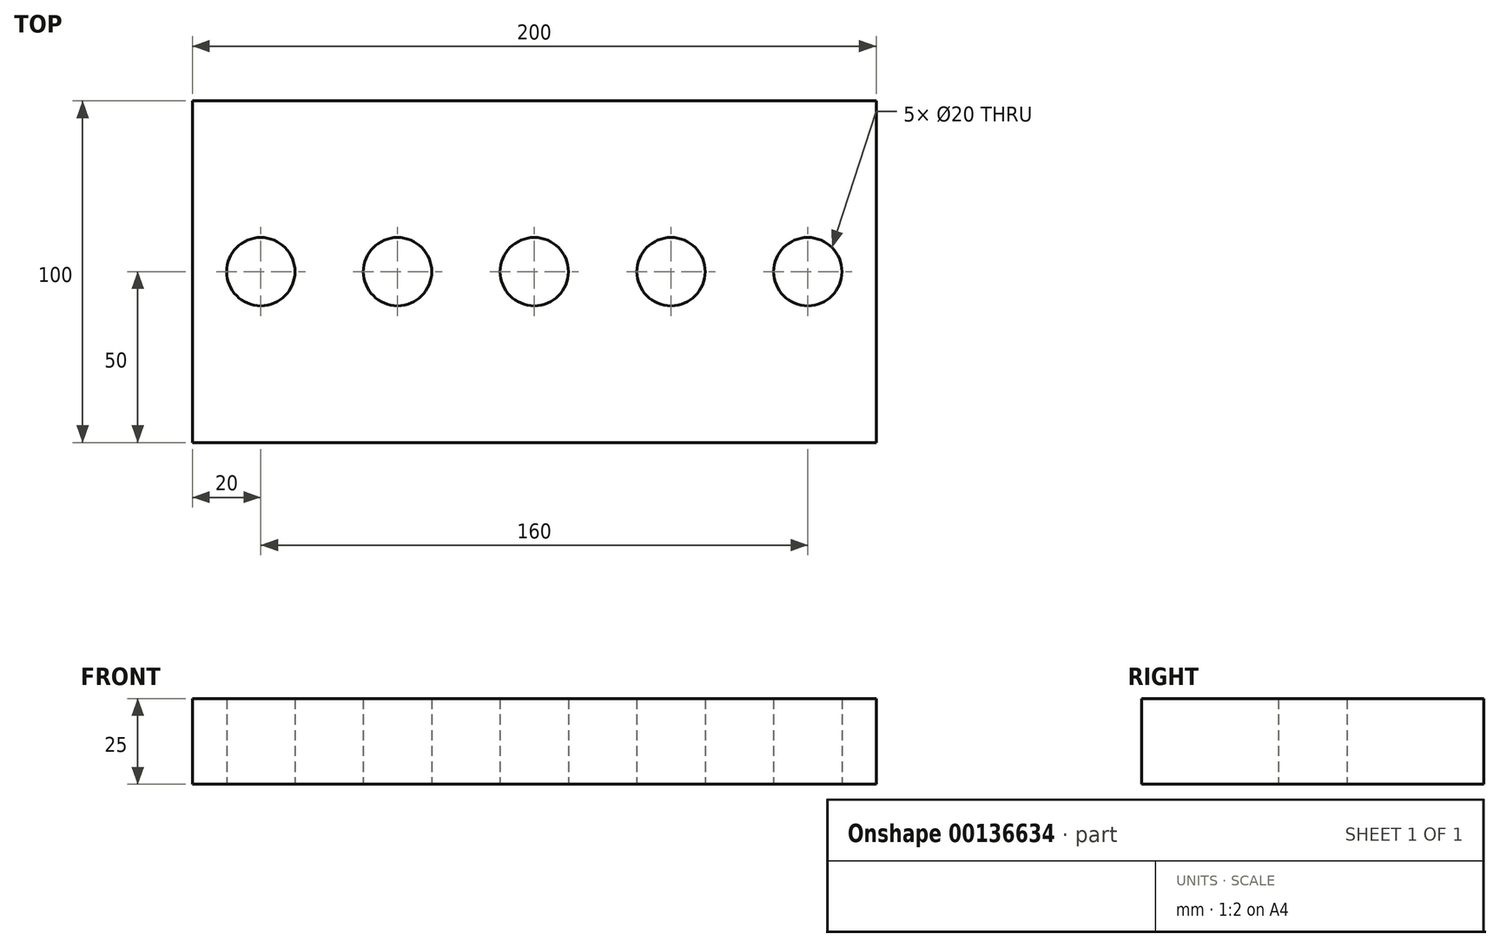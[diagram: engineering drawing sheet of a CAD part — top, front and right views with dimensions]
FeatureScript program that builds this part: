
annotation { "Feature Type Name" : "Feature", "Feature Type Description" : "" }
export const myFeature = defineFeature(function(context is Context, id is Id, definition is map)
    precondition{}
    {
        {
            var Q0;
            Q0=qCreatedBy(makeId("Top.planeOp"),FACE);
            var sketch = newSketch(context, id + "F0", { "sketchPlane" : qUnion([Q0])});
            skLineSegment(sketch, "E0.bottom", {"start": v(-100, 50) * mm, "end": v(100, 50) * mm});
            skLineSegment(sketch, "E0.top", {"start": v(-100, -50) * mm, "end": v(100, -50) * mm});
            skLineSegment(sketch, "E0.left", {"start": v(-100, 50) * mm, "end": v(-100, -50) * mm});
            skLineSegment(sketch, "E0.right", {"start": v(100, 50) * mm, "end": v(100, -50) * mm});
            skPoint(sketch, "E1", {"position": v(-80, 0) * mm});
            skPoint(sketch, "E2", {"position": v(-40, 0) * mm});
            skPoint(sketch, "E3", {"position": v(0, 0) * mm});
            skPoint(sketch, "E4", {"position": v(40, 0) * mm});
            skPoint(sketch, "E5", {"position": v(80, 0) * mm});
            skSolve(sketch);
        }
        {
            var Q0;
            Q0 = qSketchRegion(id + "F0", true);
            extrude(context, id + "F1", {"entities" : qUnion([Q0]), "depth" : 25 * mm});
        }
        {
            var Q0;
            Q0=sQuery(id+"F0.wireOp",VERTEX,"E1");
            var Q1;
            Q1=sQuery(id+"F0.wireOp",VERTEX,"E2");
            var Q2;
            Q2=sQuery(id+"F0.wireOp",VERTEX,"E3");
            var Q3;
            Q3=sQuery(id+"F0.wireOp",VERTEX,"E4");
            var Q4;
            Q4=sQuery(id+"F0.wireOp",VERTEX,"E5");
            var Q5;
            Q5=makeQuery(id+"F1.opExtrude","SWEPT_BODY",BODY,{"disambiguationData":[OSD([sQuery(id+"F0.wireOp",EDGE,"E0.bottom"),sQuery(id+"F0.wireOp",EDGE,"E0.top"),sQuery(id+"F0.wireOp",EDGE,"E0.left"),sQuery(id+"F0.wireOp",EDGE,"E0.right")])]});
            hole(context, id + "F2", {"style" : HoleStyle.SIMPLE, "endStyle" : HoleEndStyle.BLIND, "oppositeDirection" : true, "holeDiameter" : 20 * mm, "holeDepth" : 25 * mm, "locations" : qUnion([Q0, Q1, Q2, Q3, Q4]), "scope" : qUnion([Q5])});
        }
    });
